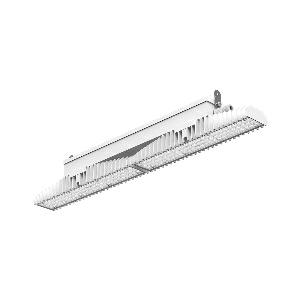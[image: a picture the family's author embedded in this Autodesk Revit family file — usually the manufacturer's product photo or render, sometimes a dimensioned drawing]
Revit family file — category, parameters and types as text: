
# Revit family: 3f_filippi_-_3f_lem_ampio_3f_filippi_-_58885_-_3f_lem_1_1_led_100_cr_ampio_9ec2
name_source: partatom
category: Lighting Fixtures
units: mm (PartAtom-declared; Revit-internal decimal feet)

## family parameters
Cut with Voids When Loaded = No
Host = Face
Light Source = No
Part Type = Normal
Room Calculation Point = No
Round Connector Dimension = Use Diameter
Shared = No

## types (1)
- 3F Filippi - 3F LEM Ampio (1 x LED, 16989 lm, 109 W, 4000 K)
    Apparent Load = 109 VA
    Approval mark = CE
    CIE Flux Codes = 60 92 99 100 100
    Color Rendering = 80
    Color Temperature = 4000 K
    Control Gear = Electronic ballast
    Default Elevation = 1800 mm
    Description = Industrial luminaire with high light output and high luminous efficiency designed with the most innovative technologies for environments with temperature up to 55°C.

ILLUMINOTECHNICAL
Luminous efficiency 100% (DLOR 100%, ULOR 0%).
Initial luminous flux of the luminaire 16989 lm.
Direct symmetric wide distribution: the illuminated area has a rectangular shape.
Installation Interdistance Transv.D = 1.58 x hu - Long.D = 1.45 x hu.
Tabular UGR (CIE 117 - 4H-8H; S=0.25H; 70/50/20): RUG 26.3 - 27.3.
Beam angle: 93° - 99°.
Luminous efficacy 156 lm/W.
Lifetime (L93/B10): 30000 h. (tq+25°C)
Lifetime (L90/B10): 50000 h. (tq+25°C)
Lifetime (L85/B10): 80000 h. (tq+25°C)
Lifetime (L80/B10): 100000 h. (tq+25°C)
Lifetime (L85/B10): 50000 h. (tq+55°C)
Sudden decreased luminous flux after 50000 hours: 0% (C0).
Photobiological safety in compliance with IEC/TR 62778: RG0 risk exempt, (IEC 62471).
In compliance with IEC/EN 62722-2-1 - IEC/EN 62717 standards.

SOURCE
2 Mid-Power linear LED modules 50W/840.
Energy efficiency class (UE 2019/2020 - UE 2019/2015): C.
CIE 13.3 Colour rendering index: CRI >80 (R9 <50%).
IES TM-30 Fidelity Index: Rf = 84 Rg = 95.
CCT nominal colour temperature 4000 K.
Colour initial tolerance (MacAdam): SDCM 3.

MECHANICAL
Passive modular heatsinks in die-casted aluminium, painted in white colour.
To optimize the thermal management of the LED module, the heatsinks are oversized and provided with self-cleaning of cooling fins.
Wiring body in aluminium and galvanised steel anchored solidly to the sinks and thermally separated.
3F Lens lenses with high luminous efficiency, transparent methacrylate (PMMA), fixed to the LED modules.
Fixing brackets in stainless steel.
Luminaire with limited surface temperature. - D - (EN 60598-2-24)
Dimensions: 1099x115 mm, height 150 mm. Weight 10.46 kg.
IP65 protection degree.
Mechanical strength to impacts IK06 (1 joule).
Glow-wire test resistance 650°C.

ELECTRICAL
Halogen Free electronic wiring 230V-50/60Hz, power factor 0.97, THD <25%, constant output current, class I, 1 driver.
Power of the luminaire 109 W.
ENEC - CE.
SAFE FLICKER: PstLM=<1 and SVM=<0.4 (IEC TR 61547-1 and IEC TR 63158), to ensure a more comfortable and safe light.
Luminaire compliant with EN 60598-2-22 for power supply from a centralised emergency system CPSS (Central Power Supply System), not incorporated in the luminaire - high risk areas excluded. The default power and flux are 100% in AC and 100% in DC.
Ambient temperature from -30°C to +55°C.
Temperature class T6 max 85°C.
Quick connection via M20 3P connector with 9-13 mm tightening range.
Power unit positioned on a separate compartment by the LED module to ensure optimum temperatures of cabling components, to be inspectable and maintainable.
Relative humidity UR: <85%.

INSTALLATION
Ceiling / Suspended / Wall.
All accessories dedicated to this product are available on the Catalog and on our website www.3F-Filippi.com.

APPLICATIONS
In commercial environments, exhibition and industrial areas, stores, open areas.
Applications with high ambient temperature up to 55°C.
Environments in which it is necessary a total protection against falling fragments (eg environments with foodstuffs or machines with moving parts or with extreme temperature changes), use luminaires with polycarbonate lenses.

WARNING
Fixture not suitable for cold stores with an ambient temperature <0°C and/or relative humidity >85%.
Luminaire designed for disposal/recycling at end-of-life.
Replaceable (LED only) light source by a professional. Replaceable control gear by a professional.
    Height = 150 mm
    Lamp = 1 x LED
    Lamp Light Flux = 16989 lm
    Lamp Power = 109 W
    Lamp count = 1
    Length = 1099 mm
    Lifetime = 50000 h
    Luminous efficacy = 156 lm/W
    Manufacturer = 3F Filippi
    ModVariant = No
    Model = 3F Filippi - 58885 - 3F LEM 1+1 LED 100 CR AMPIO
    Mounting Place = Ceiling
    Mounting Type = Pendant
    Number of Poles = 1
    OnlyDefault = Yes
    Power Factor = 1
    Product Name = 3F Filippi - 3F LEM Ampio
    Product group = pendant luminaire
    ProductGroupID = 9
    Protection Class = Protection class I
    Protection Degree = IP 65
    RLX_Detail_Level = 1
    RLX_Emergency_Light_Flux = 0 lm
    RLX_Emergency_Type = 0
    RLX_Emergency_Type_DB = No
    RlxData = <blob elided: 83257 chars, md5=de94b435>
    Socket = socket
    Standby Power = 0 W
    System Light Flux = 16989 lm
    System Power = 109 W
    Type Comments = Product without accessories
    Type Image = 3f_filippi_-_lem_11.jpg
    URL = http://relux.com
    VarID = ---
    Voltage = 0 V
    Weight = 0.00 kg
    Width = 115 mm

## geometry (parser evidence)
native form markers: Blend x4, Sweep x13
no freeform markers — native parametric forms only
